# Revit family: Supports-Teknion-CEAFSK-Side_Filler_Cabinet Kit-Expansion_Casework+-R2023
name_source: partatom
category: Furniture
units: mm (PartAtom-declared; Revit-internal decimal feet)

## family parameters
Always vertical = Yes
Cut with Voids When Loaded = No
Enable Cutting in Views = No
OmniClass Number = 23.40.20.00
OmniClass Title = General Furniture and Specialties
Render Appearance Source = Family Geometry
Room Calculation Point = No
Shared = Yes
Work Plane-Based = No

## types (3) — shared parameters
Assembly Code = E2020200
Depth = 6.701 "
Description = Side Filler - Cabinets Kit for Appliance
Manufacturer = Teknion
Manufacturer Fax = 416.661.4586
Part Number = CEASFK
Product Documentation Link = http://www.teknion.com
http://www.teknion.com
Product Line = Expansion Casework +
Product Page URL = https://www.teknion.com
Series = Accesories
Sustainability Data = https://www.teknion.com
URL = www.teknion.com
Unit Weight URL = http://www.teknion.com
Warranty = http://www.teknion.com
Width = 6 "
zero-valued in all types: Default Elevation, Length

## per-type parameters (varying)
| type | Dim1 | Height | Model |
| Height 96 -  Filler | 43.654 " | 96 " | CEASFK0696 |
| Height 90 -  Filler | 40.594 " | 90 " | CEASFK0690 |
| Height 84 -  Filler | 37.654 " | 84 " | CEASFK0684 |

## geometry (parser evidence)
native form markers: Sweep x2
no freeform markers — native parametric forms only
